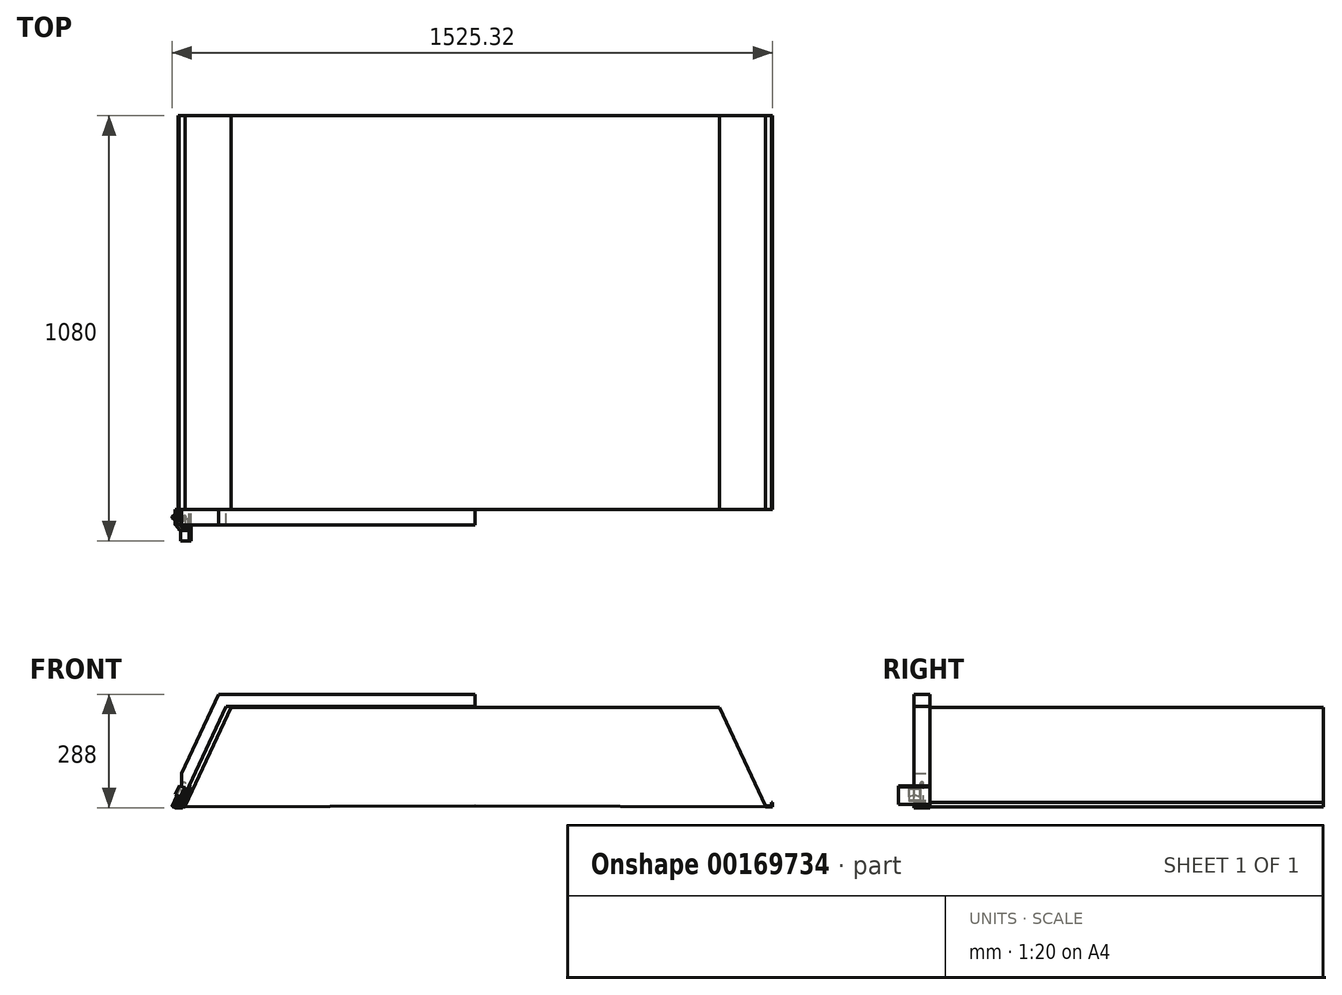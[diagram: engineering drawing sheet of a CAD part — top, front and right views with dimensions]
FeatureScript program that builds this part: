
annotation { "Feature Type Name" : "Feature", "Feature Type Description" : "" }
export const myFeature = defineFeature(function(context is Context, id is Id, definition is map)
    precondition{}
    {
        {
            var Q0;
            Q0=qCreatedBy(makeId("Front.planeOp"),FACE);
            var sketch = newSketch(context, id + "F0", { "sketchPlane" : qUnion([Q0])});
            skLineSegment(sketch, "E0", {"start": v(-755, 13.85) * mm, "end": v(-752, 13.85) * mm});
            skLineSegment(sketch, "E1", {"start": v(-752, 13.85) * mm, "end": v(-752, 5.85) * mm});
            skLineSegment(sketch, "E2", {"start": v(-752, 5.85) * mm, "end": v(-737, 5.85) * mm});
            skLineSegment(sketch, "E3", {"start": v(-755, 13.85) * mm, "end": v(-755, 2.85) * mm});
            skPoint(sketch, "E4.end.orphan", {"position": v(-737, -5.88) * mm});
            skLineSegment(sketch, "E5", {"start": v(-755, 2.85) * mm, "end": v(-737, 2.85) * mm});
            skLineSegment(sketch, "E6", {"start": v(-737, 5.85) * mm, "end": v(-620.42, 255.85) * mm});
            skLineSegment(sketch, "E7", {"start": v(-620.42, 255.85) * mm, "end": v(0, 255.85) * mm});
            skLineSegment(sketch, "E8", {"start": v(-737, 2.85) * mm, "end": v(0, 5.85) * mm});
            skLineSegment(sketch, "E9", {"start": v(0, 5.85) * mm, "end": v(0, 255.85) * mm});
            skLineSegment(sketch, "E10.MirrorCS", {"start": v(755, 2.85) * mm, "end": v(737, 2.85) * mm});
            skLineSegment(sketch, "E11.MirrorCS", {"start": v(755, 13.85) * mm, "end": v(755, 2.85) * mm});
            skLineSegment(sketch, "E12.MirrorCS", {"start": v(752, 5.85) * mm, "end": v(737, 5.85) * mm});
            skLineSegment(sketch, "E13.MirrorCS", {"start": v(752, 13.85) * mm, "end": v(752, 5.85) * mm});
            skLineSegment(sketch, "E14.MirrorCS", {"start": v(755, 13.85) * mm, "end": v(752, 13.85) * mm});
            skLineSegment(sketch, "E15.MirrorCS", {"start": v(737, 2.85) * mm, "end": v(0, 5.85) * mm});
            skLineSegment(sketch, "E16.MirrorCS", {"start": v(620.42, 255.85) * mm, "end": v(0, 255.85) * mm});
            skLineSegment(sketch, "E17.MirrorCS", {"start": v(737, 5.85) * mm, "end": v(620.42, 255.85) * mm});
            skPoint(sketch, "E18.MirrorP", {"position": v(737, -5.88) * mm});
            skSolve(sketch);
        }
        {
            var Q0;
            Q0=makeQuery(id+"F0.imprint","IMPRINT",FACE,{"disambiguationData":[TD([[makeQuery(id+"F0.imprint","IMPRINT",EDGE,{"derivedFrom":sQuery(id+"F0.wireOp",EDGE,"E0")}),-1.0]])]});
            var Q1;
            Q1=makeQuery(id+"F0.imprint","IMPRINT",FACE,{"disambiguationData":[TD([[makeQuery(id+"F0.imprint","IMPRINT",EDGE,{"derivedFrom":sQuery(id+"F0.wireOp",EDGE,"E9")}),-1.0]])]});
            extrude(context, id + "F1", {"entities" : qUnion([Q0, Q1]), "depth" : 1000 * mm});
        }
        {
            var Q0;
            Q0=makeQuery(id+"F1.opExtrude","CAP_FACE",FACE,{"disambiguationData":[OSD([sQuery(id+"F0.wireOp",EDGE,"E0"),sQuery(id+"F0.wireOp",EDGE,"E1"),sQuery(id+"F0.wireOp",EDGE,"E2"),sQuery(id+"F0.wireOp",EDGE,"E3"),sQuery(id+"F0.wireOp",EDGE,"E5"),sQuery(id+"F0.wireOp",EDGE,"E6"),sQuery(id+"F0.wireOp",EDGE,"E7"),sQuery(id+"F0.wireOp",EDGE,"E8"),sQuery(id+"F0.wireOp",EDGE,"E10.MirrorCS"),sQuery(id+"F0.wireOp",EDGE,"E11.MirrorCS"),sQuery(id+"F0.wireOp",EDGE,"E12.MirrorCS"),sQuery(id+"F0.wireOp",EDGE,"E13.MirrorCS"),sQuery(id+"F0.wireOp",EDGE,"E14.MirrorCS"),sQuery(id+"F0.wireOp",EDGE,"E15.MirrorCS"),sQuery(id+"F0.wireOp",EDGE,"E16.MirrorCS"),sQuery(id+"F0.wireOp",EDGE,"E17.MirrorCS")])],"isStart":false});
            var sketch = newSketch(context, id + "F2", { "sketchPlane" : qUnion([Q0])});
            skLineSegment(sketch, "E19", {"start": v(-721.71, 54.17) * mm, "end": v(-727.15, 56.7) * mm});
            skLineSegment(sketch, "E20", {"start": v(-727.15, 56.7) * mm, "end": v(-748.28, 11.39) * mm});
            skLineSegment(sketch, "E21", {"start": v(-748.28, 11.39) * mm, "end": v(-742.84, 8.85) * mm});
            skLineSegment(sketch, "E22", {"start": v(-721.71, 54.17) * mm, "end": v(-742.84, 8.85) * mm});
            skSolve(sketch);
        }
        {
            var Q0;
            Q0=makeQuery(id+"F2.imprint","IMPRINT",FACE,{"disambiguationData":[TD([[makeQuery(id+"F2.imprint","IMPRINT",EDGE,{"derivedFrom":sQuery(id+"F2.wireOp",EDGE,"E19")}),1.0]])]});
            extrude(context, id + "F3", {"entities" : qUnion([Q0]), "depth" : 80 * mm});
        }
        {
            var Q0;
            Q0=makeQuery(id+"F3.opExtrude","SWEPT_FACE",FACE,{"disambiguationData":[OSD([sQuery(id+"F2.wireOp",EDGE,"E20")])]});
            var sketch = newSketch(context, id + "F4", { "sketchPlane" : qUnion([Q0])});
            skLineSegment(sketch, "E23.bottom", {"start": v(1023.86, -266) * mm, "end": v(1053.86, -266) * mm});
            skLineSegment(sketch, "E23.top", {"start": v(1023.86, -300) * mm, "end": v(1053.86, -300) * mm});
            skLineSegment(sketch, "E23.left", {"start": v(1023.86, -266) * mm, "end": v(1023.86, -300) * mm});
            skLineSegment(sketch, "E23.right", {"start": v(1053.86, -266) * mm, "end": v(1053.86, -300) * mm});
            skSolve(sketch);
        }
        {
            var Q0;
            Q0=makeQuery(id+"F4.imprint","IMPRINT",FACE,{"disambiguationData":[TD([[makeQuery(id+"F4.imprint","IMPRINT",EDGE,{"derivedFrom":sQuery(id+"F4.wireOp",EDGE,"E23.bottom")}),-1.0]])]});
            extrude(context, id + "F5", {"entities" : qUnion([Q0]), "operationType" : NewBodyOperationType.ADD, "depth" : 7 * mm});
        }
        {
            var Q0;
            Q0=makeQuery(id+"F5.opExtrude","SWEPT_FACE",FACE,{"disambiguationData":[OSD([sQuery(id+"F4.wireOp",EDGE,"E23.bottom")])]});
            var sketch = newSketch(context, id + "F6", { "sketchPlane" : qUnion([Q0])});
            skLineSegment(sketch, "E24", {"start": v(-703.07, -1038.86) * mm, "end": v(-689.99, -1051.94) * mm});
            skLineSegment(sketch, "E25", {"start": v(-703.07, -1038.86) * mm, "end": v(-689.99, -1025.78) * mm});
            skLineSegment(sketch, "E26", {"start": v(-703.07, -1038.86) * mm, "end": v(-689.99, -1038.86) * mm});
            skLineSegment(sketch, "E27", {"start": v(-689.99, -1051.94) * mm, "end": v(-691.05, -1053) * mm});
            skLineSegment(sketch, "E28", {"start": v(-691.05, -1053) * mm, "end": v(-705.19, -1038.86) * mm});
            skLineSegment(sketch, "E29", {"start": v(-705.19, -1038.86) * mm, "end": v(-691.05, -1024.72) * mm});
            skLineSegment(sketch, "E30", {"start": v(-689.99, -1025.78) * mm, "end": v(-691.05, -1024.72) * mm});
            skSolve(sketch);
        }
        {
            var Q0;
            Q0=makeQuery(id+"F6.imprint","IMPRINT",FACE,{"disambiguationData":[TD([[makeQuery(id+"F6.imprint","IMPRINT",EDGE,{"derivedFrom":sQuery(id+"F6.wireOp",EDGE,"E24")}),-1.0]])]});
            extrude(context, id + "F7", {"entities" : qUnion([Q0]), "oppositeDirection" : true, "depth" : 25 * mm});
        }
        {
            var Q0;
            Q0=makeQuery(id+"F1.opExtrude","CAP_FACE",FACE,{"disambiguationData":[OSD([sQuery(id+"F0.wireOp",EDGE,"E0"),sQuery(id+"F0.wireOp",EDGE,"E1"),sQuery(id+"F0.wireOp",EDGE,"E2"),sQuery(id+"F0.wireOp",EDGE,"E3"),sQuery(id+"F0.wireOp",EDGE,"E5"),sQuery(id+"F0.wireOp",EDGE,"E6"),sQuery(id+"F0.wireOp",EDGE,"E7"),sQuery(id+"F0.wireOp",EDGE,"E8"),sQuery(id+"F0.wireOp",EDGE,"E10.MirrorCS"),sQuery(id+"F0.wireOp",EDGE,"E11.MirrorCS"),sQuery(id+"F0.wireOp",EDGE,"E12.MirrorCS"),sQuery(id+"F0.wireOp",EDGE,"E13.MirrorCS"),sQuery(id+"F0.wireOp",EDGE,"E14.MirrorCS"),sQuery(id+"F0.wireOp",EDGE,"E15.MirrorCS"),sQuery(id+"F0.wireOp",EDGE,"E16.MirrorCS"),sQuery(id+"F0.wireOp",EDGE,"E17.MirrorCS")])],"isStart":false});
            var sketch = newSketch(context, id + "F8", { "sketchPlane" : qUnion([Q0])});
            skLineSegment(sketch, "E31", {"start": v(-754.74, 18.97) * mm, "end": v(-763.2, 0.85) * mm});
            skLineSegment(sketch, "E32", {"start": v(-763.2, 0.85) * mm, "end": v(-743.2, 0.85) * mm});
            skLineSegment(sketch, "E33", {"start": v(-743.2, 0.85) * mm, "end": v(-743.2, 2.35) * mm});
            skLineSegment(sketch, "E34", {"start": v(-743.2, 2.35) * mm, "end": v(-761, 2.35) * mm});
            skLineSegment(sketch, "E35", {"start": v(-754.74, 18.97) * mm, "end": v(-753.5, 18.4) * mm});
            skLineSegment(sketch, "E36", {"start": v(-753.5, 18.4) * mm, "end": v(-761, 2.35) * mm});
            skSolve(sketch);
        }
        {
            var Q0;
            Q0=makeQuery(id+"F8.imprint","IMPRINT",FACE,{"disambiguationData":[TD([[makeQuery(id+"F8.imprint","IMPRINT",EDGE,{"derivedFrom":sQuery(id+"F8.wireOp",EDGE,"E31")}),1.0]])]});
            extrude(context, id + "F9", {"entities" : qUnion([Q0]), "depth" : 40 * mm});
        }
        {
            var Q0;
            Q0=makeQuery(id+"F9.opExtrude","SWEPT_FACE",FACE,{"disambiguationData":[OSD([sQuery(id+"F8.wireOp",EDGE,"E35")])]});
            var sketch = newSketch(context, id + "F10", { "sketchPlane" : qUnion([Q0])});
            skCircle(sketch, "E37", {"center": v(-696.05, -1019.93) * mm, "radius": 4 * mm});
            skSolve(sketch);
        }
        {
            var Q0;
            Q0 = qSketchRegion(id + "F10", true);
            extrude(context, id + "F11", {"entities" : qUnion([Q0]), "operationType" : NewBodyOperationType.ADD, "oppositeDirection" : true, "depth" : 19.7 * mm, "hasSecondDirection" : true, "secondDirectionOppositeDirection" : false, "secondDirectionDepth" : 48.1 * mm});
        }
        {
            var Q0;
            Q0=makeQuery(id+"F1.opExtrude","CAP_FACE",FACE,{"disambiguationData":[OSD([sQuery(id+"F0.wireOp",EDGE,"E0"),sQuery(id+"F0.wireOp",EDGE,"E1"),sQuery(id+"F0.wireOp",EDGE,"E2"),sQuery(id+"F0.wireOp",EDGE,"E3"),sQuery(id+"F0.wireOp",EDGE,"E5"),sQuery(id+"F0.wireOp",EDGE,"E6"),sQuery(id+"F0.wireOp",EDGE,"E7"),sQuery(id+"F0.wireOp",EDGE,"E8"),sQuery(id+"F0.wireOp",EDGE,"E10.MirrorCS"),sQuery(id+"F0.wireOp",EDGE,"E11.MirrorCS"),sQuery(id+"F0.wireOp",EDGE,"E12.MirrorCS"),sQuery(id+"F0.wireOp",EDGE,"E13.MirrorCS"),sQuery(id+"F0.wireOp",EDGE,"E14.MirrorCS"),sQuery(id+"F0.wireOp",EDGE,"E15.MirrorCS"),sQuery(id+"F0.wireOp",EDGE,"E16.MirrorCS"),sQuery(id+"F0.wireOp",EDGE,"E17.MirrorCS")])],"isStart":false});
            var sketch = newSketch(context, id + "F12", { "sketchPlane" : qUnion([Q0])});
            skLineSegment(sketch, "E38", {"start": v(0, 258.85) * mm, "end": v(0, 288.85) * mm});
            skLineSegment(sketch, "E39", {"start": v(-652, 288.85) * mm, "end": v(0, 288.85) * mm});
            skLineSegment(sketch, "E40", {"start": v(-632.89, 258.85) * mm, "end": v(0, 258.85) * mm});
            skLineSegment(sketch, "E41", {"start": v(-652, 288.85) * mm, "end": v(-745.72, 87.88) * mm});
            skLineSegment(sketch, "E42", {"start": v(-745.72, 16.89) * mm, "end": v(-745.72, 87.88) * mm});
            skLineSegment(sketch, "E43", {"start": v(-632.89, 258.85) * mm, "end": v(-745.72, 16.89) * mm});
            skLineSegment(sketch, "E44", {"start": v(-652, 288.85) * mm, "end": v(-632.89, 258.85) * mm});
            skLineSegment(sketch, "E45", {"start": v(-632.89, 258.85) * mm, "end": v(-654.16, 258.85) * mm});
            skLineSegment(sketch, "E46", {"start": v(-745.72, 16.89) * mm, "end": v(-774.16, 30.15) * mm});
            skSolve(sketch);
        }
        {
            var Q0;
            Q0 = qSketchRegion(id + "F12", true);
            extrude(context, id + "F13", {"entities" : qUnion([Q0]), "depth" : 40 * mm});
        }
    });
